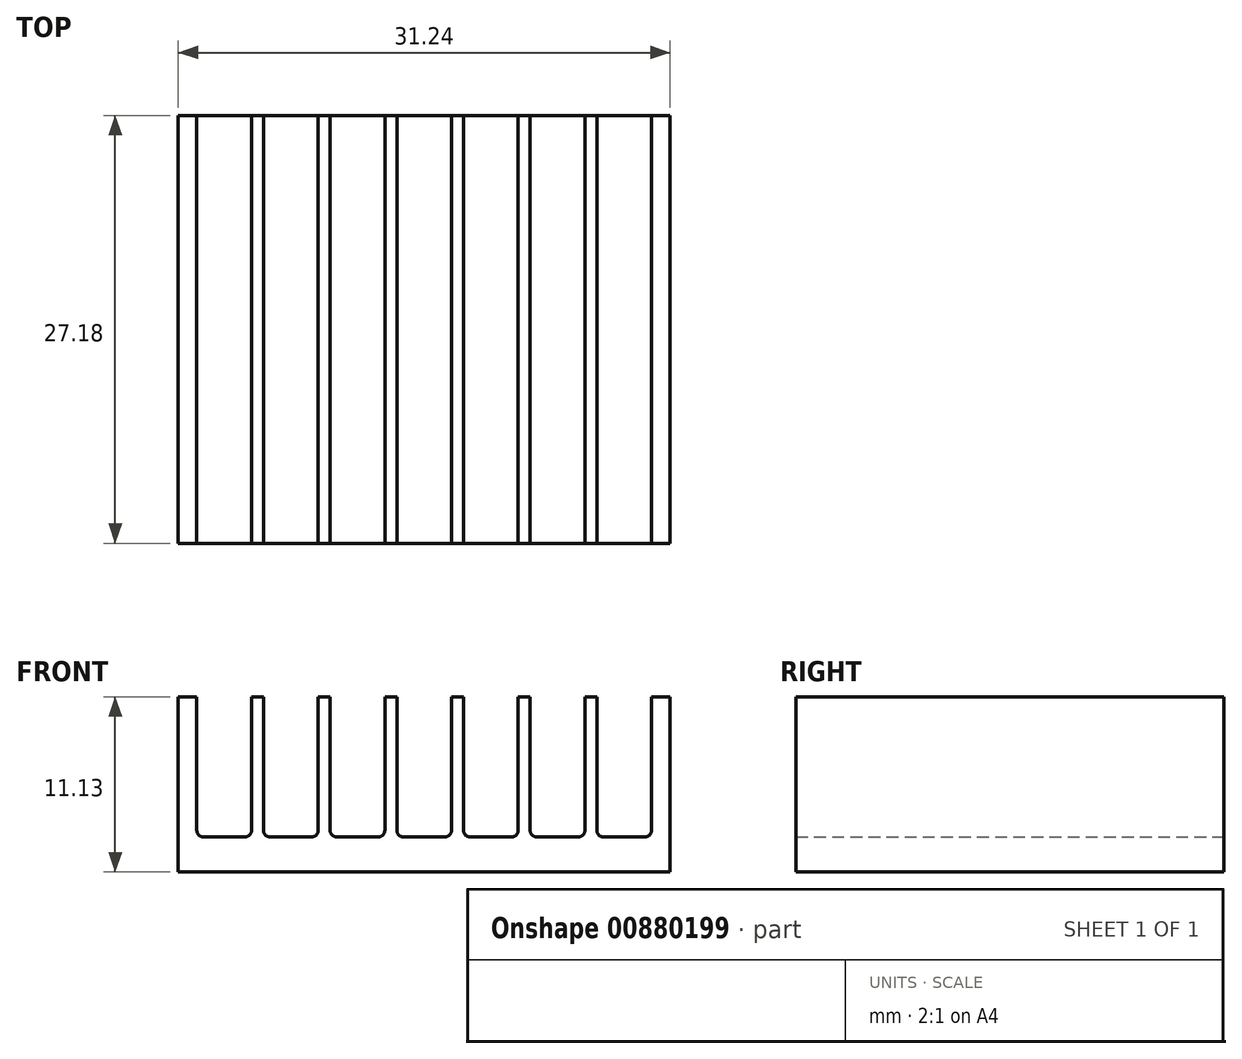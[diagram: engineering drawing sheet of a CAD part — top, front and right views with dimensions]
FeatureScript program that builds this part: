
annotation { "Feature Type Name" : "Feature", "Feature Type Description" : "" }
export const myFeature = defineFeature(function(context is Context, id is Id, definition is map)
    precondition{}
    {
        {
            var Q0;
            Q0=qCreatedBy(makeId("Front.planeOp"),FACE);
            var sketch = newSketch(context, id + "F0", { "sketchPlane" : qUnion([Q0])});
            skLineSegment(sketch, "E0", {"start": v(31.24, 0) * mm, "end": v(0, 0) * mm});
            skLineSegment(sketch, "E1", {"start": v(0, 0) * mm, "end": v(0, 11.13) * mm});
            skLineSegment(sketch, "E2", {"start": v(0, 11.13) * mm, "end": v(1.18, 11.13) * mm});
            skLineSegment(sketch, "E3", {"start": v(1.18, 11.13) * mm, "end": v(1.18, 2.24) * mm});
            skLineSegment(sketch, "E4", {"start": v(1.18, 2.24) * mm, "end": v(4.65, 2.24) * mm});
            skLineSegment(sketch, "E5", {"start": v(4.65, 2.24) * mm, "end": v(4.65, 11.13) * mm});
            skLineSegment(sketch, "E6", {"start": v(4.65, 11.13) * mm, "end": v(5.42, 11.13) * mm});
            skLineSegment(sketch, "E7", {"start": v(5.42, 11.13) * mm, "end": v(5.42, 2.24) * mm});
            skLineSegment(sketch, "E8", {"start": v(5.42, 2.24) * mm, "end": v(8.89, 2.24) * mm});
            skLineSegment(sketch, "E9", {"start": v(8.89, 2.24) * mm, "end": v(8.89, 11.13) * mm});
            skLineSegment(sketch, "E10", {"start": v(8.89, 11.13) * mm, "end": v(9.65, 11.13) * mm});
            skLineSegment(sketch, "E11", {"start": v(9.65, 11.13) * mm, "end": v(9.65, 2.24) * mm});
            skLineSegment(sketch, "E12", {"start": v(9.65, 2.24) * mm, "end": v(13.12, 2.24) * mm});
            skLineSegment(sketch, "E13", {"start": v(13.12, 2.24) * mm, "end": v(13.12, 11.13) * mm});
            skLineSegment(sketch, "E14", {"start": v(13.12, 11.13) * mm, "end": v(13.88, 11.13) * mm});
            skLineSegment(sketch, "E15", {"start": v(13.88, 11.13) * mm, "end": v(13.88, 2.24) * mm});
            skLineSegment(sketch, "E16", {"start": v(13.88, 2.24) * mm, "end": v(17.36, 2.24) * mm});
            skLineSegment(sketch, "E17", {"start": v(17.36, 2.24) * mm, "end": v(17.36, 11.13) * mm});
            skLineSegment(sketch, "E18", {"start": v(17.36, 11.13) * mm, "end": v(18.12, 11.13) * mm});
            skLineSegment(sketch, "E19", {"start": v(18.12, 11.13) * mm, "end": v(18.12, 2.24) * mm});
            skLineSegment(sketch, "E20", {"start": v(25.83, 2.24) * mm, "end": v(25.83, 11.13) * mm});
            skLineSegment(sketch, "E21", {"start": v(25.83, 11.13) * mm, "end": v(26.59, 11.13) * mm});
            skLineSegment(sketch, "E22", {"start": v(26.59, 11.13) * mm, "end": v(26.59, 2.24) * mm});
            skLineSegment(sketch, "E23", {"start": v(21.6, 2.24) * mm, "end": v(21.6, 11.13) * mm});
            skLineSegment(sketch, "E24", {"start": v(21.6, 11.13) * mm, "end": v(22.35, 11.13) * mm});
            skLineSegment(sketch, "E25", {"start": v(18.12, 2.24) * mm, "end": v(21.6, 2.24) * mm});
            skLineSegment(sketch, "E26", {"start": v(31.24, 11.13) * mm, "end": v(30.06, 11.13) * mm});
            skLineSegment(sketch, "E27", {"start": v(30.06, 11.13) * mm, "end": v(30.06, 2.24) * mm});
            skLineSegment(sketch, "E28", {"start": v(26.59, 2.24) * mm, "end": v(30.06, 2.24) * mm});
            skLineSegment(sketch, "E29", {"start": v(31.24, 0) * mm, "end": v(31.24, 11.13) * mm});
            skLineSegment(sketch, "E30", {"start": v(22.35, 11.13) * mm, "end": v(22.35, 2.24) * mm});
            skLineSegment(sketch, "E31", {"start": v(22.35, 2.24) * mm, "end": v(25.83, 2.24) * mm});
            skLineSegment(sketch, "E32", {"start": v(0, 11.13) * mm, "end": v(31.24, 11.13) * mm, "construction": true});
            skSolve(sketch);
        }
        {
            var Q0;
            Q0 = qSketchRegion(id + "F0", true);
            extrude(context, id + "F1", {"entities" : qUnion([Q0]), "depth" : 27.18 * mm, "offsetDistance" : 25.4 * mm});
        }
        {
            var Q0;
            Q0=makeQuery(id+"F1.opExtrude","SWEPT_EDGE",EDGE,{"disambiguationData":[OSD([sQuery(id+"F0.wireOp",EDGE,"E3"),sQuery(id+"F0.wireOp",EDGE,"E4")])]});
            var Q1;
            Q1=makeQuery(id+"F1.opExtrude","SWEPT_EDGE",EDGE,{"disambiguationData":[OSD([sQuery(id+"F0.wireOp",EDGE,"E4"),sQuery(id+"F0.wireOp",EDGE,"E5")])]});
            var Q2;
            Q2=makeQuery(id+"F1.opExtrude","SWEPT_EDGE",EDGE,{"disambiguationData":[OSD([sQuery(id+"F0.wireOp",EDGE,"E7"),sQuery(id+"F0.wireOp",EDGE,"E8")])]});
            var Q3;
            Q3=makeQuery(id+"F1.opExtrude","SWEPT_EDGE",EDGE,{"disambiguationData":[OSD([sQuery(id+"F0.wireOp",EDGE,"E8"),sQuery(id+"F0.wireOp",EDGE,"E9")])]});
            var Q4;
            Q4=makeQuery(id+"F1.opExtrude","SWEPT_EDGE",EDGE,{"disambiguationData":[OSD([sQuery(id+"F0.wireOp",EDGE,"E11"),sQuery(id+"F0.wireOp",EDGE,"E12")])]});
            var Q5;
            Q5=makeQuery(id+"F1.opExtrude","SWEPT_EDGE",EDGE,{"disambiguationData":[OSD([sQuery(id+"F0.wireOp",EDGE,"E12"),sQuery(id+"F0.wireOp",EDGE,"E13")])]});
            var Q6;
            Q6=makeQuery(id+"F1.opExtrude","SWEPT_EDGE",EDGE,{"disambiguationData":[OSD([sQuery(id+"F0.wireOp",EDGE,"E15"),sQuery(id+"F0.wireOp",EDGE,"E16")])]});
            var Q7;
            Q7=makeQuery(id+"F1.opExtrude","SWEPT_EDGE",EDGE,{"disambiguationData":[OSD([sQuery(id+"F0.wireOp",EDGE,"E16"),sQuery(id+"F0.wireOp",EDGE,"E17")])]});
            var Q8;
            Q8=makeQuery(id+"F1.opExtrude","SWEPT_EDGE",EDGE,{"disambiguationData":[OSD([sQuery(id+"F0.wireOp",EDGE,"E19"),sQuery(id+"F0.wireOp",EDGE,"E25")])]});
            var Q9;
            Q9=makeQuery(id+"F1.opExtrude","SWEPT_EDGE",EDGE,{"disambiguationData":[OSD([sQuery(id+"F0.wireOp",EDGE,"E23"),sQuery(id+"F0.wireOp",EDGE,"E25")])]});
            var Q10;
            Q10=makeQuery(id+"F1.opExtrude","SWEPT_EDGE",EDGE,{"disambiguationData":[OSD([sQuery(id+"F0.wireOp",EDGE,"E30"),sQuery(id+"F0.wireOp",EDGE,"E31")])]});
            var Q11;
            Q11=makeQuery(id+"F1.opExtrude","SWEPT_EDGE",EDGE,{"disambiguationData":[OSD([sQuery(id+"F0.wireOp",EDGE,"E20"),sQuery(id+"F0.wireOp",EDGE,"E31")])]});
            var Q12;
            Q12=makeQuery(id+"F1.opExtrude","SWEPT_EDGE",EDGE,{"disambiguationData":[OSD([sQuery(id+"F0.wireOp",EDGE,"E22"),sQuery(id+"F0.wireOp",EDGE,"E28")])]});
            var Q13;
            Q13=makeQuery(id+"F1.opExtrude","SWEPT_EDGE",EDGE,{"disambiguationData":[OSD([sQuery(id+"F0.wireOp",EDGE,"E27"),sQuery(id+"F0.wireOp",EDGE,"E28")])]});
            fillet(context, id + "F2", {"entities" : qUnion([Q0, Q1, Q2, Q3, Q4, Q5, Q6, Q7, Q8, Q9, Q10, Q11, Q12, Q13]), "radius" : 0.4 * mm, "tangentPropagation" : true, "allowEdgeOverflow" : false});
        }
    });
